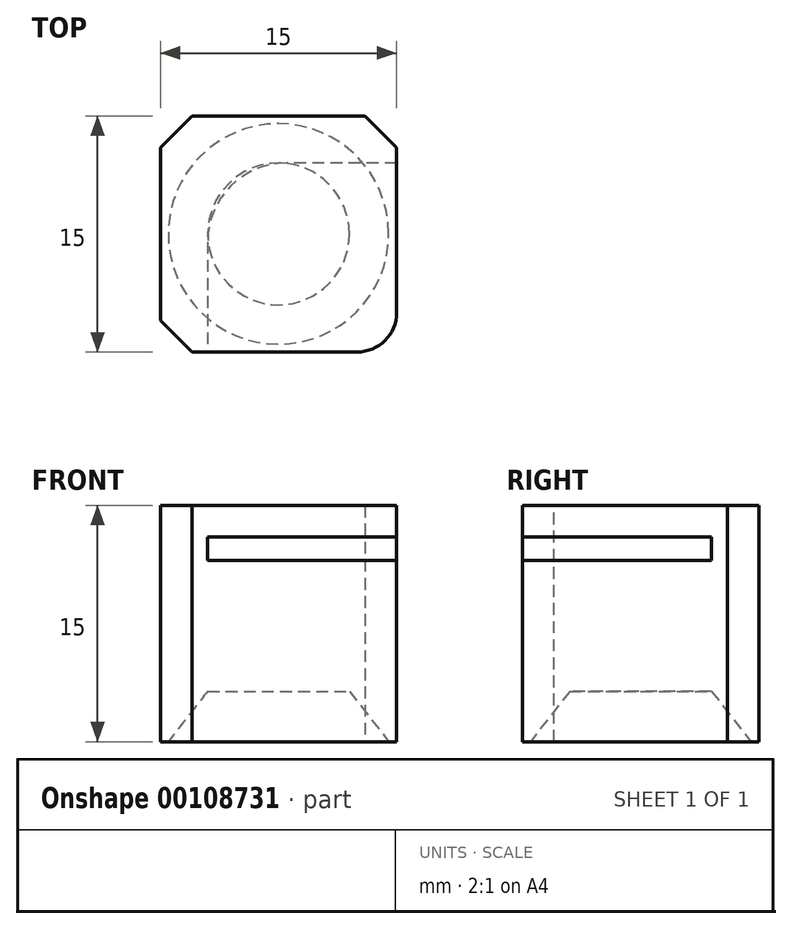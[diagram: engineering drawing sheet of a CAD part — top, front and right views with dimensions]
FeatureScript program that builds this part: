
annotation { "Feature Type Name" : "Feature", "Feature Type Description" : "" }
export const myFeature = defineFeature(function(context is Context, id is Id, definition is map)
    precondition{}
    {
        {
            var Q0;
            Q0=qCreatedBy(makeId("Top.planeOp"),FACE);
            var sketch = newSketch(context, id + "F0", { "sketchPlane" : qUnion([Q0])});
            skLineSegment(sketch, "E0.bottom", {"start": v(0, 0) * mm, "end": v(15, 0) * mm});
            skLineSegment(sketch, "E0.top", {"start": v(0, 15) * mm, "end": v(15, 15) * mm});
            skLineSegment(sketch, "E0.left", {"start": v(0, 0) * mm, "end": v(0, 15) * mm});
            skLineSegment(sketch, "E0.right", {"start": v(15, 0) * mm, "end": v(15, 15) * mm});
            skPoint(sketch, "E1.visualSharp", {"position": v(0, 15) * mm});
            skSolve(sketch);
        }
        {
            var Q0;
            Q0 = qSketchRegion(id + "F0", true);
            extrude(context, id + "F1", {"entities" : qUnion([Q0]), "depth" : 15 * mm});
        }
        {
            var Q0;
            Q0=makeQuery(id+"F1.opExtrude","SWEPT_FACE",FACE,{"disambiguationData":[OSD([sQuery(id+"F0.wireOp",EDGE,"E0.bottom")])]});
            var sketch = newSketch(context, id + "F2", { "sketchPlane" : qUnion([Q0])});
            skLineSegment(sketch, "E2.bottom", {"start": v(15, 13) * mm, "end": v(3, 13) * mm});
            skLineSegment(sketch, "E2.top", {"start": v(15, 11.52) * mm, "end": v(3, 11.52) * mm});
            skLineSegment(sketch, "E2.left", {"start": v(15, 13) * mm, "end": v(15, 11.52) * mm});
            skLineSegment(sketch, "E2.right", {"start": v(3, 13) * mm, "end": v(3, 11.52) * mm});
            skSolve(sketch);
        }
        {
            var Q0;
            Q0=makeQuery(id+"F2.imprint","IMPRINT",FACE,{"disambiguationData":[TD([[makeQuery(id+"F2.imprint","IMPRINT",EDGE,{"derivedFrom":sQuery(id+"F2.wireOp",EDGE,"E2.bottom")}),1.0]])]});
            extrude(context, id + "F3", {"entities" : qUnion([Q0]), "operationType" : NewBodyOperationType.REMOVE, "oppositeDirection" : true, "depth" : 12 * mm});
        }
        {
            var Q0;
            Q0=makeQuery(id+"F3.boolean.opBoolean","COPY",EDGE,{"derivedFrom":makeQuery(id+"F3.opExtrude","CAP_EDGE",EDGE,{"disambiguationData":[OSD([sQuery(id+"F2.wireOp",EDGE,"E2.right")])],"isStart":false})});
            fillet(context, id + "F4", {"entities" : qUnion([Q0]), "radius" : 5 * mm, "tangentPropagation" : true, "allowEdgeOverflow" : false});
        }
        {
            var Q0;
            Q0=makeQuery(id+"F1.opExtrude","CAP_FACE",FACE,{"disambiguationData":[OSD([sQuery(id+"F0.wireOp",EDGE,"E0.bottom"),sQuery(id+"F0.wireOp",EDGE,"E0.top"),sQuery(id+"F0.wireOp",EDGE,"E0.left"),sQuery(id+"F0.wireOp",EDGE,"E0.right")])],"isStart":true});
            var sketch = newSketch(context, id + "F5", { "sketchPlane" : qUnion([Q0])});
            skCircle(sketch, "E3", {"center": v(7.5, -7.5) * mm, "radius": 7 * mm});
            skLineSegment(sketch, "E4", {"start": v(7.5, 0) * mm, "end": v(7.5, -15) * mm, "construction": true});
            skSolve(sketch);
        }
        {
            var Q0;
            Q0 = qSketchRegion(id + "F5", true);
            extrude(context, id + "F6", {"entities" : qUnion([Q0]), "operationType" : NewBodyOperationType.REMOVE, "oppositeDirection" : true, "depth" : 3.2 * mm});
        }
        {
            var Q0;
            Q0=makeQuery(id+"F6.boolean.opBoolean","COPY",EDGE,{"derivedFrom":makeQuery(id+"F6.opExtrude","CAP_EDGE",EDGE,{"disambiguationData":[OSD([sQuery(id+"F5.wireOp",EDGE,"E3")])],"isStart":false})});
            chamfer(context, id + "F7", {"entities" : qUnion([Q0]), "chamferType" : ChamferType.TWO_OFFSETS, "width1" : 2.5 * mm, "oppositeDirection" : false, "width2" : 3.2 * mm, "tangentPropagation" : true});
        }
        {
            var Q0;
            {var subQ0=sQuery(id+"F0.wireOp",EDGE,"E0.bottom");var subQ1=sQuery(id+"F0.wireOp",EDGE,"E0.right");Q0=makeQuery(id+"F3.boolean.opBoolean","SPLIT",EDGE,{"disambiguationData":[TD([makeQuery(id+"F3.opExtrude","SWEPT_FACE",FACE,{"disambiguationData":[OSD([sQuery(id+"F2.wireOp",EDGE,"E2.bottom")])]})])],"derivedFrom":makeQuery(id+"F1.opExtrude","SWEPT_EDGE",EDGE,{"disambiguationData":[OSD([subQ0,subQ1])]})});}
            var Q1;
            {var subQ0=sQuery(id+"F0.wireOp",EDGE,"E0.bottom");var subQ1=sQuery(id+"F0.wireOp",EDGE,"E0.right");Q1=makeQuery(id+"F3.boolean.opBoolean","SPLIT",EDGE,{"disambiguationData":[TD([makeQuery(id+"F3.opExtrude","SWEPT_FACE",FACE,{"disambiguationData":[OSD([sQuery(id+"F2.wireOp",EDGE,"E2.top")])]})])],"derivedFrom":makeQuery(id+"F1.opExtrude","SWEPT_EDGE",EDGE,{"disambiguationData":[OSD([subQ0,subQ1])]})});}
            fillet(context, id + "F8", {"entities" : qUnion([Q0, Q1]), "radius" : 2.5 * mm, "tangentPropagation" : true, "allowEdgeOverflow" : false});
        }
        {
            var Q0;
            Q0=makeQuery(id+"F1.opExtrude","SWEPT_EDGE",EDGE,{"disambiguationData":[OSD([sQuery(id+"F0.wireOp",EDGE,"E0.top"),sQuery(id+"F0.wireOp",EDGE,"E0.right")])]});
            var Q1;
            Q1=makeQuery(id+"F1.opExtrude","SWEPT_EDGE",EDGE,{"disambiguationData":[OSD([sQuery(id+"F0.wireOp",EDGE,"E0.top"),sQuery(id+"F0.wireOp",EDGE,"E0.left")])]});
            var Q2;
            Q2=makeQuery(id+"F1.opExtrude","SWEPT_EDGE",EDGE,{"disambiguationData":[OSD([sQuery(id+"F0.wireOp",EDGE,"E0.bottom"),sQuery(id+"F0.wireOp",EDGE,"E0.left")])]});
            chamfer(context, id + "F9", {"entities" : qUnion([Q0, Q1, Q2]), "width" : 2 * mm, "tangentPropagation" : true});
        }
    });
